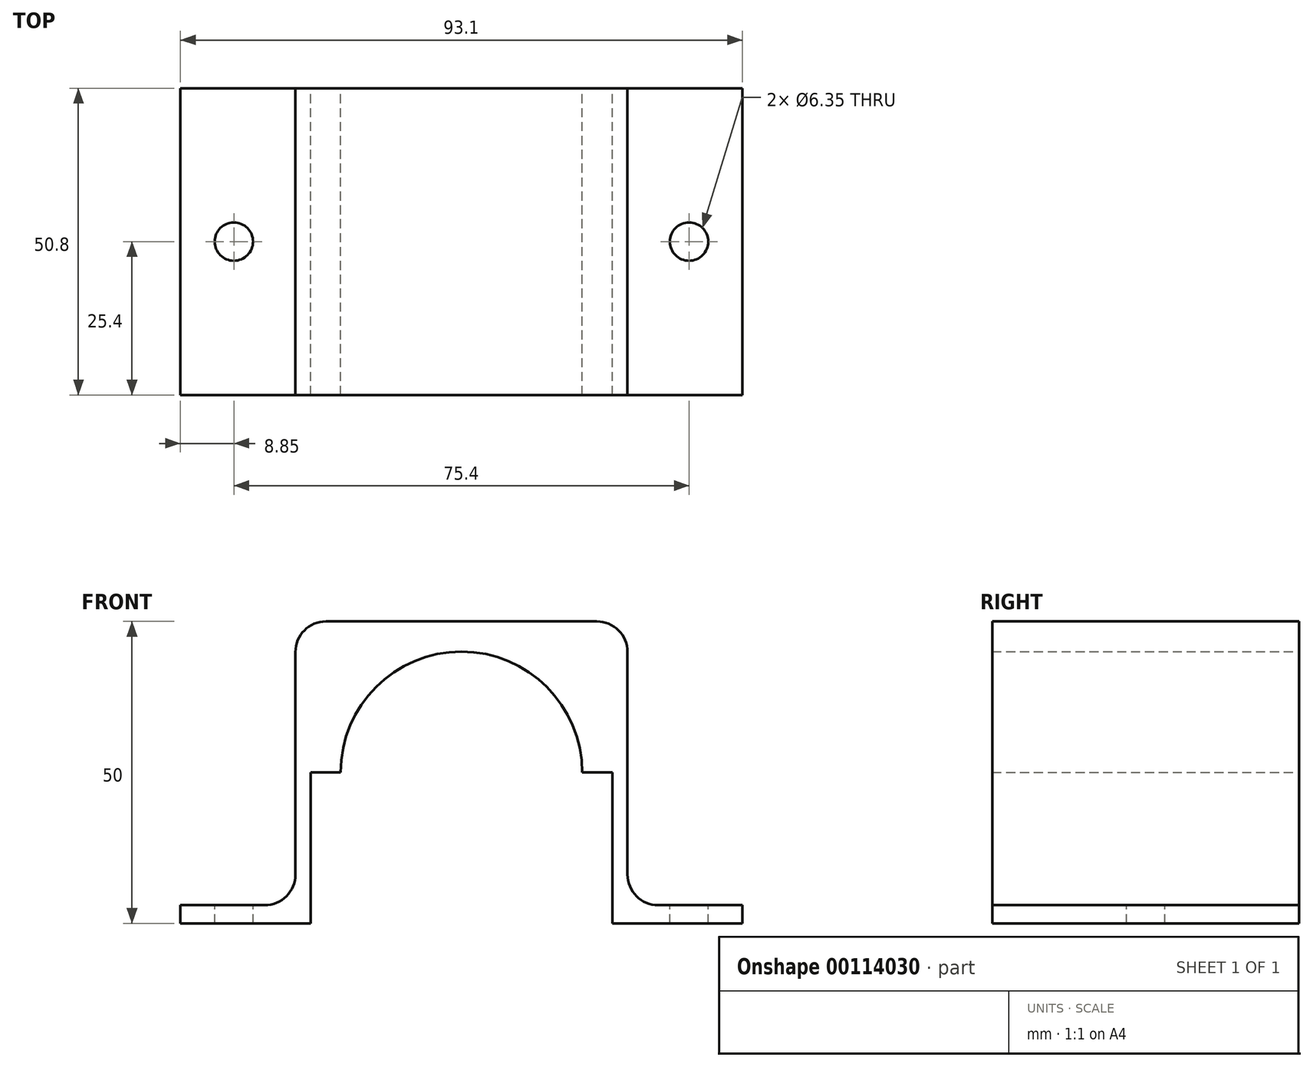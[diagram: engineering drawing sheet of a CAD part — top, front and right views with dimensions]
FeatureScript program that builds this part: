
annotation { "Feature Type Name" : "Feature", "Feature Type Description" : "" }
export const myFeature = defineFeature(function(context is Context, id is Id, definition is map)
    precondition{}
    {
        {
            var Q0;
            Q0=qCreatedBy(makeId("Front.planeOp"),FACE);
            var sketch = newSketch(context, id + "F0", { "sketchPlane" : qUnion([Q0])});
            skLineSegment(sketch, "E0.bottom", {"start": v(-25, 0) * mm, "end": v(-20, 0) * mm});
            skLineSegment(sketch, "E0.top", {"start": v(-27.5, 25) * mm, "end": v(27.5, 25) * mm});
            skLineSegment(sketch, "E0.left", {"start": v(-27.5, 0) * mm, "end": v(-27.5, 25) * mm});
            skLineSegment(sketch, "E0.right", {"start": v(27.5, 0) * mm, "end": v(27.5, 25) * mm});
            skArc(sketch, "E1", {"start": v(20, 0) * mm, "mid": v(0, 20) * mm, "end": v(-20, 0) * mm});
            skLineSegment(sketch, "E2.trimOffspring", {"start": v(20, 0) * mm, "end": v(25, 0) * mm});
            skLineSegment(sketch, "E3", {"start": v(-25, 0) * mm, "end": v(-25, -25) * mm});
            skLineSegment(sketch, "E4", {"start": v(-25, -25) * mm, "end": v(-46.55, -25) * mm});
            skLineSegment(sketch, "E5", {"start": v(25, 0) * mm, "end": v(25, -25) * mm});
            skLineSegment(sketch, "E6", {"start": v(-27.5, 0) * mm, "end": v(-27.5, -22) * mm});
            skLineSegment(sketch, "E7", {"start": v(-27.5, -22) * mm, "end": v(-46.55, -22) * mm});
            skLineSegment(sketch, "E8", {"start": v(-46.55, -22) * mm, "end": v(-46.55, -25) * mm});
            skLineSegment(sketch, "E9", {"start": v(25, -25) * mm, "end": v(46.55, -25) * mm});
            skLineSegment(sketch, "E10", {"start": v(46.55, -25) * mm, "end": v(46.55, -22) * mm});
            skLineSegment(sketch, "E11", {"start": v(46.55, -22) * mm, "end": v(27.5, -22) * mm});
            skLineSegment(sketch, "E12", {"start": v(27.5, -22) * mm, "end": v(27.5, 0) * mm});
            skSolve(sketch);
        }
        {
            var Q0;
            Q0=makeQuery(id+"F0.imprint","IMPRINT",FACE,{"disambiguationData":[TD([[makeQuery(id+"F0.imprint","IMPRINT",EDGE,{"derivedFrom":sQuery(id+"F0.wireOp",EDGE,"E0.bottom")}),-1.0]])]});
            var Q1;
            Q1=makeQuery(id+"F0.imprint","IMPRINT",FACE,{"disambiguationData":[TD([[makeQuery(id+"F0.imprint","IMPRINT",EDGE,{"derivedFrom":sQuery(id+"F0.wireOp",EDGE,"E0.bottom")}),1.0]])]});
            var Q2;
            Q2=makeQuery(id+"F0.imprint","IMPRINT",FACE,{"disambiguationData":[TD([[makeQuery(id+"F0.imprint","IMPRINT",EDGE,{"derivedFrom":sQuery(id+"F0.wireOp",EDGE,"E2.trimOffspring")}),-1.0]])]});
            extrude(context, id + "F1", {"entities" : qUnion([Q0, Q1, Q2]), "depth" : 50.8 * mm});
        }
        {
            var Q0;
            Q0=makeQuery(id+"F1.opExtrude","SWEPT_EDGE",EDGE,{"disambiguationData":[OSD([sQuery(id+"F0.wireOp",EDGE,"E0.top"),sQuery(id+"F0.wireOp",EDGE,"E0.left")])]});
            var Q1;
            Q1=makeQuery(id+"F1.opExtrude","SWEPT_EDGE",EDGE,{"disambiguationData":[OSD([sQuery(id+"F0.wireOp",EDGE,"E0.top"),sQuery(id+"F0.wireOp",EDGE,"E0.right")])]});
            fillet(context, id + "F2", {"entities" : qUnion([Q0, Q1]), "radius" : 5.08 * mm, "tangentPropagation" : true, "allowEdgeOverflow" : false});
        }
        {
            var Q0;
            Q0=makeQuery(id+"F1.opExtrude","SWEPT_EDGE",EDGE,{"disambiguationData":[OSD([sQuery(id+"F0.wireOp",EDGE,"E6"),sQuery(id+"F0.wireOp",EDGE,"E7")])]});
            var Q1;
            Q1=makeQuery(id+"F1.opExtrude","SWEPT_EDGE",EDGE,{"disambiguationData":[OSD([sQuery(id+"F0.wireOp",EDGE,"E11"),sQuery(id+"F0.wireOp",EDGE,"E12")])]});
            fillet(context, id + "F3", {"entities" : qUnion([Q0, Q1]), "radius" : 5.08 * mm, "tangentPropagation" : true, "allowEdgeOverflow" : false});
        }
        {
            var Q0;
            Q0=makeQuery(id+"F1.opExtrude","SWEPT_FACE",FACE,{"disambiguationData":[OSD([sQuery(id+"F0.wireOp",EDGE,"E7")])]});
            var sketch = newSketch(context, id + "F4", { "sketchPlane" : qUnion([Q0])});
            skCircle(sketch, "E13", {"center": v(-37.7, -25.4) * mm, "radius": 3.18 * mm});
            skPoint(sketch, "E13.centerSnap0", {"position": v(-25, -25.4) * mm});
            skCircle(sketch, "E14", {"center": v(37.7, -25.4) * mm, "radius": 3.18 * mm});
            skSolve(sketch);
        }
        {
            var Q0;
            Q0 = qSketchRegion(id + "F4", true);
            extrude(context, id + "F5", {"entities" : qUnion([Q0]), "operationType" : NewBodyOperationType.REMOVE, "oppositeDirection" : true, "depth" : 25.4 * mm});
        }
    });
